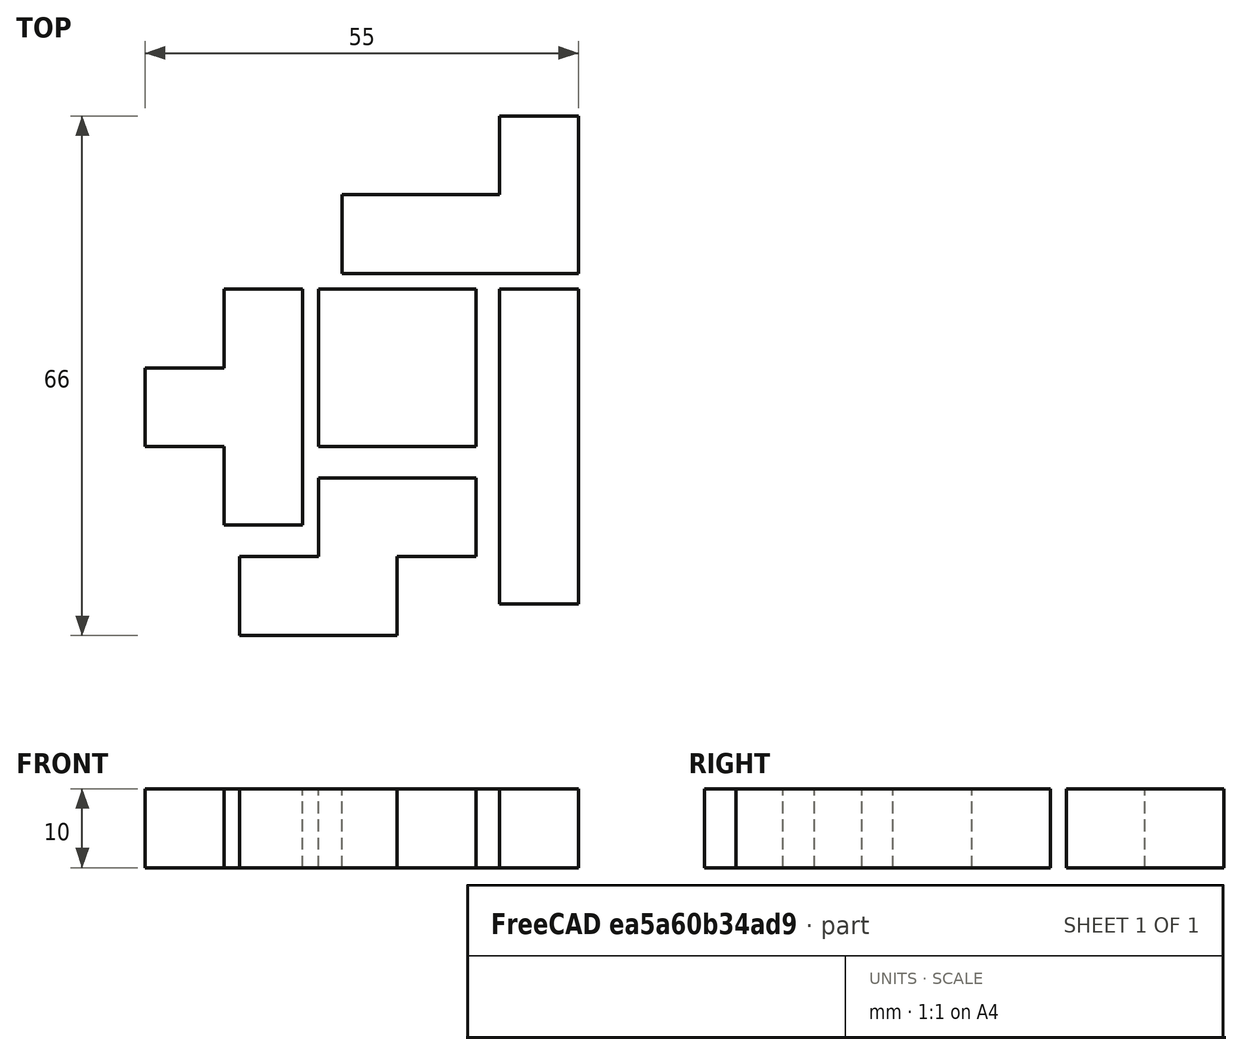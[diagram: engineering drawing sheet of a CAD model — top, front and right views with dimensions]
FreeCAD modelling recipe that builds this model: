
FCSTD DOCUMENT  (FreeCAD 0.21R33694 (Git))
Label: OJT1_T05P02_TETRIS
License: All rights reserved
LicenseURL: http://en.wikipedia.org/wiki/All_rights_reserved
objects: Part::Box×20, Part::MultiFuse×9, Part::Fuse×5
note: 34 computed .brp shape members not serialized (recipe doc carries the construction recipe); baked Part::Feature solids carry a one-line shape summary decoded from their .brp

FEATURE [Part::Box] Box  label="Cub"
  AttacherType = Attacher::AttachEngine3D
  Height = 10
  Length = 10
  Placement = pos=(0,-20,0) rot=(0,0,1;0rad)
  Width = 10
FEATURE [Part::Box] Box001  label="Cub001"
  AttacherType = Attacher::AttachEngine3D
  Height = 10
  Length = 10
  Placement = pos=(0,10,0) rot=(0,0,1;0rad)
  Width = 10
FEATURE [Part::Box] Box002  label="Cub002"
  AttacherType = Attacher::AttachEngine3D
  Height = 10
  Length = 10
  Width = 10
FEATURE [Part::Box] Box003  label="Cub003"
  AttacherType = Attacher::AttachEngine3D
  Height = 10
  Length = 10
  Placement = pos=(0,-10,0) rot=(0,0,1;0rad)
  Width = 10
FEATURE [Part::Fuse] Fusion
  Base = -> Box
  Refine = true
  Tool = -> Box001
FEATURE [Part::Fuse] Fusion001
  Base = -> Box
  Refine = true
  Tool = -> Box001
FEATURE [Part::Fuse] Fusion002
  Base = -> Box002
  Refine = true
  Tool = -> Box003
FEATURE [Part::Fuse] Fusion003
  Base = -> Fusion002
  Refine = true
  Tool = -> Fusion
FEATURE [Part::MultiFuse] Fusion004
  Placement = pos=(21,0,0) rot=(0,0,1;0rad)
  Refine = true
  Shapes = -> [Fusion003,Fusion001]
FEATURE [Part::Box] Box004  label="Cub004"
  AttacherType = Attacher::AttachEngine3D
  Height = 10
  Length = 10
  Placement = pos=(0,-10,0) rot=(0,0,1;0rad)
  Width = 10
FEATURE [Part::Box] Box005  label="Cub005"
  AttacherType = Attacher::AttachEngine3D
  Height = 10
  Length = 10
  Placement = pos=(-10,0,0) rot=(0,0,1;0rad)
  Width = 10
FEATURE [Part::Box] Box006  label="Cub006"
  AttacherType = Attacher::AttachEngine3D
  Height = 10
  Length = 10
  Placement = pos=(-10,10,0) rot=(0,0,1;0rad)
  Width = 10
FEATURE [Part::Box] Box007  label="Cub007"
  AttacherType = Attacher::AttachEngine3D
  Height = 10
  Length = 10
  Width = 10
FEATURE [Part::Fuse] Fusion005
  Base = -> Box004
  Refine = true
  Tool = -> Box005
FEATURE [Part::MultiFuse] Fusion006
  Refine = true
  Shapes = -> [Fusion005,Box007]
FEATURE [Part::MultiFuse] Fusion007
  Placement = pos=(8,-14,0) rot=(0,0,1;1.5708rad)
  Refine = true
  Shapes = -> [Box006,Fusion006]
FEATURE [Part::Box] Box008  label="Cub008"
  AttacherType = Attacher::AttachEngine3D
  Height = 10
  Length = 10
  Placement = pos=(0,-10,0) rot=(0,0,1;0rad)
  Width = 10
FEATURE [Part::Box] Box009  label="Cub009"
  AttacherType = Attacher::AttachEngine3D
  Height = 10
  Length = 10
  Placement = pos=(0,-20,0) rot=(0,0,1;0rad)
  Width = 10
FEATURE [Part::Box] Box010  label="Cub010"
  AttacherType = Attacher::AttachEngine3D
  Height = 10
  Length = 10
  Placement = pos=(-10,0,0) rot=(0,0,1;0rad)
  Width = 10
FEATURE [Part::Box] Box011  label="Cub011"
  AttacherType = Attacher::AttachEngine3D
  Height = 10
  Length = 10
  Width = 10
FEATURE [Part::MultiFuse] Fusion008
  Refine = true
  Shapes = -> [Box008,Box009]
FEATURE [Part::MultiFuse] Fusion009
  Refine = true
  Shapes = -> [Box011,Box010]
FEATURE [Part::MultiFuse] Fusion010
  Placement = pos=(21,32,0) rot=(0,0,1;4.71239rad)
  Refine = true
  Shapes = -> [Fusion008,Fusion009]
FEATURE [Part::Box] Box012  label="Cub012"
  AttacherType = Attacher::AttachEngine3D
  Height = 10
  Length = 10
  Placement = pos=(0,-10,0) rot=(0,0,1;0rad)
  Width = 10
FEATURE [Part::Box] Box013  label="Cub013"
  AttacherType = Attacher::AttachEngine3D
  Height = 10
  Length = 10
  Placement = pos=(0,10,0) rot=(0,0,1;0rad)
  Width = 10
FEATURE [Part::Box] Box014  label="Cub014"
  AttacherType = Attacher::AttachEngine3D
  Height = 10
  Length = 10
  Placement = pos=(-10,0,0) rot=(0,0,1;0rad)
  Width = 10
FEATURE [Part::Box] Box015  label="Cub015"
  AttacherType = Attacher::AttachEngine3D
  Height = 10
  Length = 10
  Width = 10
FEATURE [Part::MultiFuse] Fusion011
  Refine = true
  Shapes = -> [Box015,Box013,Box014]
FEATURE [Part::MultiFuse] Fusion012
  Placement = pos=(-14,0,0) rot=(0,0,1;0rad)
  Refine = true
  Shapes = -> [Fusion011,Box012]
FEATURE [Part::Box] Box016  label="Cub016"
  AttacherType = Attacher::AttachEngine3D
  Height = 10
  Length = 10
  Placement = pos=(0,-10,0) rot=(0,0,1;0rad)
  Width = 10
FEATURE [Part::Box] Box017  label="Cub017"
  AttacherType = Attacher::AttachEngine3D
  Height = 10
  Length = 10
  Placement = pos=(-10,0,0) rot=(0,0,1;0rad)
  Width = 10
FEATURE [Part::Box] Box018  label="Cub018"
  AttacherType = Attacher::AttachEngine3D
  Height = 10
  Length = 10
  Placement = pos=(-10,-10,0) rot=(0,0,1;0rad)
  Width = 10
FEATURE [Part::Box] Box019  label="Cub019"
  AttacherType = Attacher::AttachEngine3D
  Height = 10
  Length = 10
  Width = 10
FEATURE [Part::MultiFuse] Fusion013
  Placement = pos=(8,10,0) rot=(0,0,1;0rad)
  Refine = true
  Shapes = -> [Box016,Box017,Box018,Box019]
